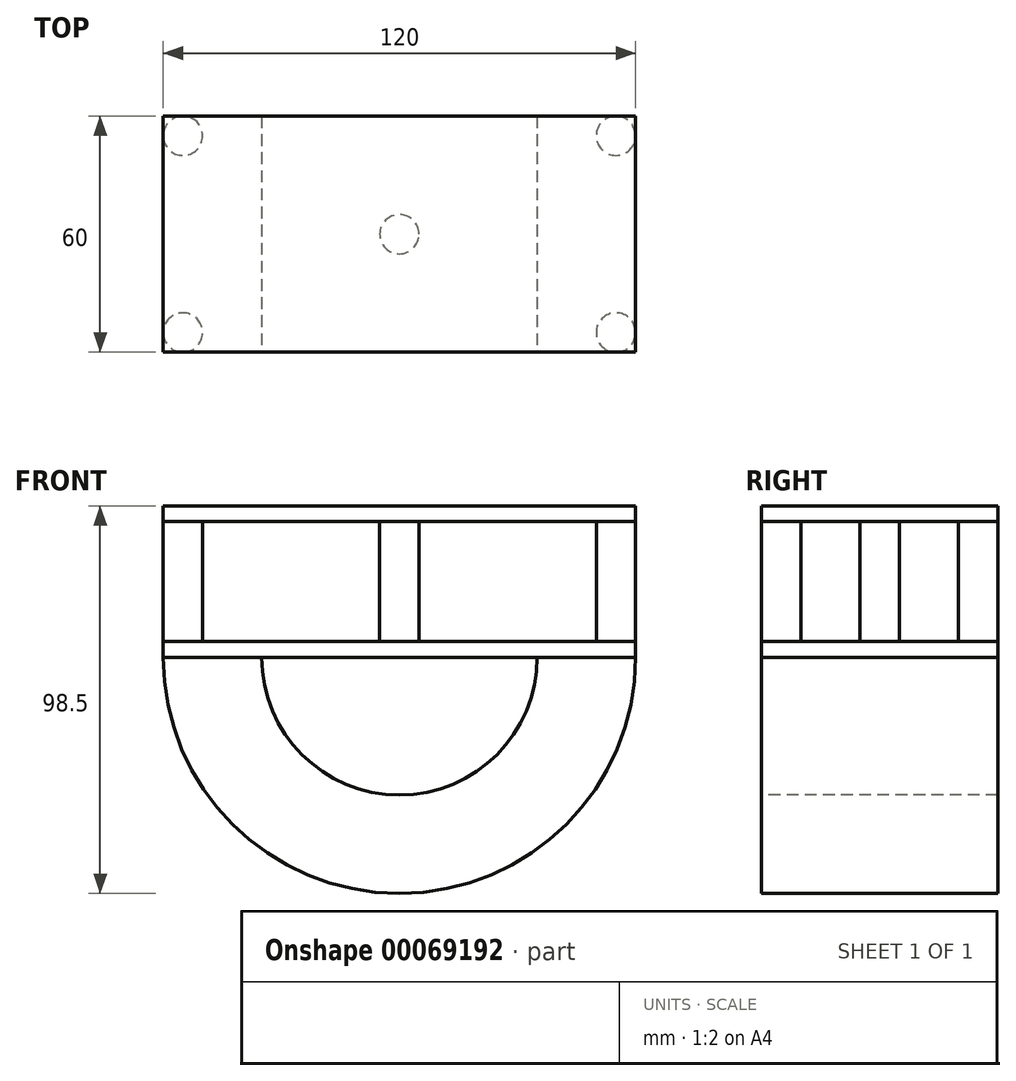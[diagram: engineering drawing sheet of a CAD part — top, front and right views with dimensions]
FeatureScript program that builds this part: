
annotation { "Feature Type Name" : "Feature", "Feature Type Description" : "" }
export const myFeature = defineFeature(function(context is Context, id is Id, definition is map)
    precondition{}
    {
        {
            var Q0;
            Q0=qCreatedBy(makeId("Top.planeOp"),FACE);
            var sketch = newSketch(context, id + "F0", { "sketchPlane" : qUnion([Q0])});
            skLineSegment(sketch, "E0.bottom", {"start": v(0, 0) * mm, "end": v(120, 0) * mm});
            skLineSegment(sketch, "E0.top", {"start": v(0, 60) * mm, "end": v(120, 60) * mm});
            skLineSegment(sketch, "E0.left", {"start": v(0, 0) * mm, "end": v(0, 60) * mm});
            skLineSegment(sketch, "E0.right", {"start": v(120, 0) * mm, "end": v(120, 60) * mm});
            skSolve(sketch);
        }
        {
            var Q0;
            Q0=makeQuery(id+"F0.imprint","IMPRINT",FACE,{"disambiguationData":[TD([[makeQuery(id+"F0.imprint","IMPRINT",EDGE,{"derivedFrom":sQuery(id+"F0.wireOp",EDGE,"E0.bottom")}),1.0]])]});
            extrude(context, id + "F1", {"entities" : qUnion([Q0]), "depth" : 4 * mm});
        }
        {
            var Q0;
            Q0=makeQuery(id+"F1.opExtrude","CAP_FACE",FACE,{"disambiguationData":[OSD([sQuery(id+"F0.wireOp",EDGE,"E0.bottom"),sQuery(id+"F0.wireOp",EDGE,"E0.top"),sQuery(id+"F0.wireOp",EDGE,"E0.left"),sQuery(id+"F0.wireOp",EDGE,"E0.right")])],"isStart":false});
            var sketch = newSketch(context, id + "F2", { "sketchPlane" : qUnion([Q0])});
            skLineSegment(sketch, "E1", {"start": v(60, 60) * mm, "end": v(60, 0) * mm, "construction": true});
            skCircle(sketch, "E2", {"center": v(60, 30) * mm, "radius": 5 * mm});
            skSolve(sketch);
        }
        {
            var Q0;
            Q0 = qSketchRegion(id + "F2", true);
            extrude(context, id + "F3", {"entities" : qUnion([Q0]), "operationType" : NewBodyOperationType.ADD, "depth" : 30.5 * mm});
        }
        {
            var Q0;
            Q0=makeQuery(id+"F1.opExtrude","CAP_FACE",FACE,{"disambiguationData":[OSD([sQuery(id+"F0.wireOp",EDGE,"E0.bottom"),sQuery(id+"F0.wireOp",EDGE,"E0.top"),sQuery(id+"F0.wireOp",EDGE,"E0.left"),sQuery(id+"F0.wireOp",EDGE,"E0.right")])],"isStart":false});
            var sketch = newSketch(context, id + "F4", { "sketchPlane" : qUnion([Q0])});
            skCircle(sketch, "E3", {"center": v(5, 55) * mm, "radius": 5 * mm});
            skLineSegment(sketch, "E4", {"start": v(5, 55) * mm, "end": v(0, 55) * mm, "construction": true});
            skLineSegment(sketch, "E5", {"start": v(120, 55) * mm, "end": v(115, 55) * mm, "construction": true});
            skCircle(sketch, "E6", {"center": v(115, 55) * mm, "radius": 5 * mm});
            skLineSegment(sketch, "E7", {"start": v(5, 0) * mm, "end": v(5, 5) * mm});
            skPoint(sketch, "E8", {"position": v(115, 5) * mm});
            skCircle(sketch, "E9", {"center": v(115, 5) * mm, "radius": 5 * mm});
            skCircle(sketch, "E10", {"center": v(5, 5) * mm, "radius": 5 * mm});
            skSolve(sketch);
        }
        {
            var Q0;
            {var subQ0=sQuery(id+"F4.wireOp",EDGE,"E3");var subQ1=makeQuery(id+"F4.imprint","INTERSECT",VERTEX,{"derivedFrom":[makeQuery(id+"F1.opExtrude","CAP_EDGE",EDGE,{"disambiguationData":[OSD([sQuery(id+"F0.wireOp",EDGE,"E0.top")])],"isStart":false}),subQ0]});Q0=makeQuery(id+"F4.imprint","IMPRINT",FACE,{"disambiguationData":[TD([[makeQuery(id+"F4.imprint","IMPRINT",EDGE,{"disambiguationData":[TD([[subQ1,-1.0]])],"derivedFrom":subQ0}),1.0]])]});}
            var Q1;
            {var subQ0=sQuery(id+"F4.wireOp",EDGE,"E10");var subQ1=makeQuery(id+"F4.imprint","INTERSECT",VERTEX,{"derivedFrom":[makeQuery(id+"F1.opExtrude","CAP_EDGE",EDGE,{"disambiguationData":[OSD([sQuery(id+"F0.wireOp",EDGE,"E0.bottom")])],"isStart":false}),subQ0]});Q1=makeQuery(id+"F4.imprint","IMPRINT",FACE,{"disambiguationData":[TD([[makeQuery(id+"F4.imprint","IMPRINT",EDGE,{"disambiguationData":[TD([[subQ1,1.0]])],"derivedFrom":subQ0}),1.0]])]});}
            var Q2;
            {var subQ0=sQuery(id+"F4.wireOp",EDGE,"E6");var subQ1=makeQuery(id+"F4.imprint","INTERSECT",VERTEX,{"derivedFrom":[makeQuery(id+"F1.opExtrude","CAP_EDGE",EDGE,{"disambiguationData":[OSD([sQuery(id+"F0.wireOp",EDGE,"E0.top")])],"isStart":false}),subQ0]});Q2=makeQuery(id+"F4.imprint","IMPRINT",FACE,{"disambiguationData":[TD([[makeQuery(id+"F4.imprint","IMPRINT",EDGE,{"disambiguationData":[TD([[subQ1,1.0]])],"derivedFrom":subQ0}),1.0]])]});}
            var Q3;
            {var subQ0=sQuery(id+"F4.wireOp",EDGE,"E9");var subQ1=makeQuery(id+"F4.imprint","INTERSECT",VERTEX,{"derivedFrom":[makeQuery(id+"F1.opExtrude","CAP_EDGE",EDGE,{"disambiguationData":[OSD([sQuery(id+"F0.wireOp",EDGE,"E0.bottom")])],"isStart":false}),subQ0]});Q3=makeQuery(id+"F4.imprint","IMPRINT",FACE,{"disambiguationData":[TD([[makeQuery(id+"F4.imprint","IMPRINT",EDGE,{"disambiguationData":[TD([[subQ1,1.0]])],"derivedFrom":subQ0}),1.0]])]});}
            extrude(context, id + "F5", {"entities" : qUnion([Q0, Q1, Q2, Q3]), "operationType" : NewBodyOperationType.ADD, "depth" : 30.5 * mm});
        }
        {
            var Q0;
            Q0=makeQuery(id+"F5.opExtrude","CAP_FACE",FACE,{"disambiguationData":[OSD([sQuery(id+"F4.wireOp",EDGE,"E3")])],"isStart":false});
            var sketch = newSketch(context, id + "F6", { "sketchPlane" : qUnion([Q0])});
            skLineSegment(sketch, "E11.bottom", {"start": v(0, 0) * mm, "end": v(120, 0) * mm});
            skLineSegment(sketch, "E11.top", {"start": v(0, 60) * mm, "end": v(120, 60) * mm});
            skLineSegment(sketch, "E11.left", {"start": v(0, 0) * mm, "end": v(0, 60) * mm});
            skLineSegment(sketch, "E11.right", {"start": v(120, 0) * mm, "end": v(120, 60) * mm});
            skSolve(sketch);
        }
        {
            var Q0;
            {var subQ1=sQuery(id+"F6.wireOp",EDGE,"E11.bottom");Q0=makeQuery(id+"F6.imprint","IMPRINT",FACE,{"disambiguationData":[TD([[makeQuery(id+"F6.imprint","IMPRINT",EDGE,{"derivedFrom":subQ1}),1.0]])]});}
            var Q1;
            {var subQ0=sQuery(id+"F6.wireOp",EDGE,"E11.left");var subQ1=sQuery(id+"F6.wireOp",EDGE,"E11.top");var subQ2=makeQuery(id+"F6.imprint","INTERSECT",VERTEX,{"derivedFrom":[subQ1,subQ0]});Q1=makeQuery(id+"F6.imprint","IMPRINT",FACE,{"disambiguationData":[TD([[makeQuery(id+"F6.imprint","IMPRINT",EDGE,{"disambiguationData":[TD([[subQ2,-1.0]])],"derivedFrom":subQ1}),-1.0]])]});}
            var Q2;
            {var subQ0=makeQuery(id+"F5.opExtrude","CAP_EDGE",EDGE,{"disambiguationData":[OSD([sQuery(id+"F4.wireOp",EDGE,"E3")])],"isStart":false});var subQ1=makeQuery(id+"F6.imprint","INTERSECT",VERTEX,{"derivedFrom":[subQ0,sQuery(id+"F6.wireOp",EDGE,"E11.top")]});Q2=makeQuery(id+"F6.imprint","IMPRINT",FACE,{"disambiguationData":[TD([[makeQuery(id+"F6.imprint","IMPRINT",EDGE,{"disambiguationData":[TD([[subQ1,1.0]])],"derivedFrom":subQ0}),1.0]])]});}
            extrude(context, id + "F7", {"entities" : qUnion([Q0, Q1, Q2]), "operationType" : NewBodyOperationType.ADD, "depth" : 4 * mm});
        }
        {
            var Q0;
            Q0=makeQuery(id+"F1.opExtrude","CAP_FACE",FACE,{"disambiguationData":[OSD([sQuery(id+"F0.wireOp",EDGE,"E0.bottom"),sQuery(id+"F0.wireOp",EDGE,"E0.top"),sQuery(id+"F0.wireOp",EDGE,"E0.left"),sQuery(id+"F0.wireOp",EDGE,"E0.right")])],"isStart":true});
            var sketch = newSketch(context, id + "F8", { "sketchPlane" : qUnion([Q0])});
            skLineSegment(sketch, "E12", {"start": v(0, 0) * mm, "end": v(120, 0) * mm});
            skPoint(sketch, "E13", {"position": v(60, 0) * mm});
            skSolve(sketch);
        }
        {
            var Q0;
            Q0=qCreatedBy(makeId("Front.planeOp"),FACE);
            var sketch = newSketch(context, id + "F9", { "sketchPlane" : qUnion([Q0])});
            skArc(sketch, "E14", {"start": v(25, 0) * mm, "mid": v(60, -35) * mm, "end": v(95, 0) * mm});
            skArc(sketch, "E15", {"start": v(0, 0) * mm, "mid": v(60, -60) * mm, "end": v(120, 0) * mm});
            skLineSegment(sketch, "E16", {"start": v(0, 0) * mm, "end": v(25, 0) * mm});
            skLineSegment(sketch, "E17", {"start": v(95, 0) * mm, "end": v(120, 0) * mm});
            skSolve(sketch);
        }
        {
            var Q0;
            Q0=makeQuery(id+"F9.imprint","IMPRINT",FACE,{"disambiguationData":[TD([[makeQuery(id+"F9.imprint","IMPRINT",EDGE,{"derivedFrom":sQuery(id+"F9.wireOp",EDGE,"E14")}),-1.0]])]});
            extrude(context, id + "F10", {"entities" : qUnion([Q0]), "oppositeDirection" : true, "depth" : 60 * mm});
        }
    });
